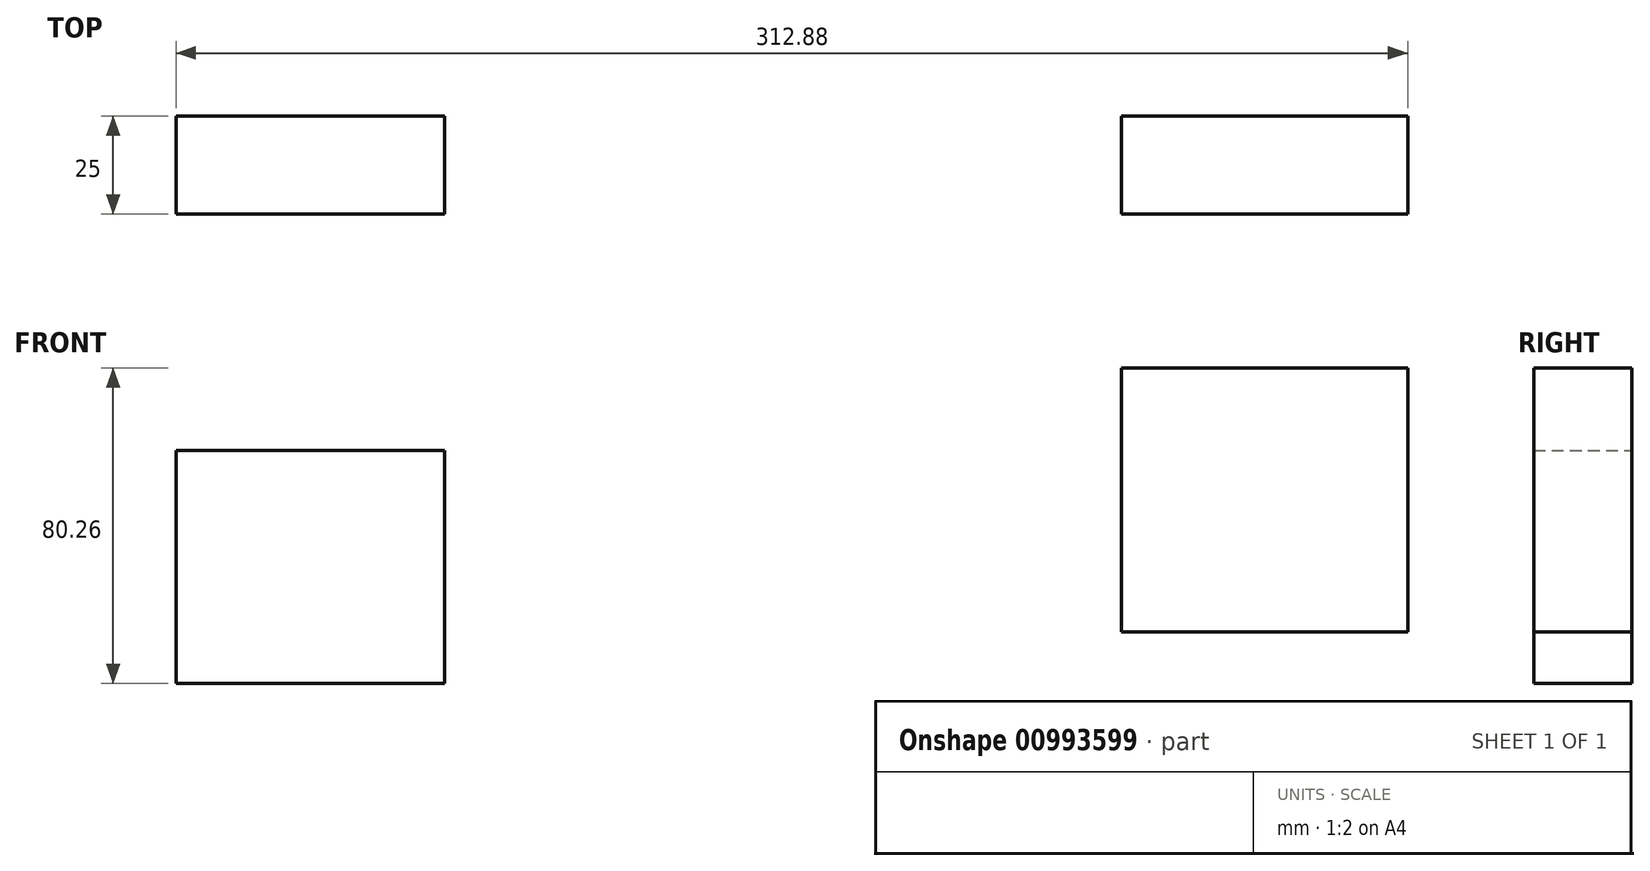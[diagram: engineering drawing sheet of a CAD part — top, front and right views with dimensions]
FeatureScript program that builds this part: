
annotation { "Feature Type Name" : "Feature", "Feature Type Description" : "" }
export const myFeature = defineFeature(function(context is Context, id is Id, definition is map)
    precondition{}
    {
        {
            var Q0;
            Q0=qCreatedBy(makeId("Front.planeOp"),FACE);
            var sketch = newSketch(context, id + "F0", { "sketchPlane" : qUnion([Q0])});
            skLineSegment(sketch, "E0.bottom", {"start": v(-157.25, 3.45) * mm, "end": v(-89.1, 3.45) * mm});
            skLineSegment(sketch, "E0.top", {"start": v(-157.25, 62.72) * mm, "end": v(-89.1, 62.72) * mm});
            skLineSegment(sketch, "E0.left", {"start": v(-157.25, 3.45) * mm, "end": v(-157.25, 62.72) * mm});
            skLineSegment(sketch, "E0.right", {"start": v(-89.1, 3.45) * mm, "end": v(-89.1, 62.72) * mm});
            skPoint(sketch, "E0.middle", {"position": v(-123.17, 33.09) * mm});
            skLineSegment(sketch, "E1.bottom", {"start": v(82.92, 16.64) * mm, "end": v(155.63, 16.64) * mm});
            skLineSegment(sketch, "E1.top", {"start": v(82.92, 83.7) * mm, "end": v(155.63, 83.7) * mm});
            skLineSegment(sketch, "E1.left", {"start": v(82.92, 16.64) * mm, "end": v(82.92, 83.7) * mm});
            skLineSegment(sketch, "E1.right", {"start": v(155.63, 16.64) * mm, "end": v(155.63, 83.7) * mm});
            skPoint(sketch, "E1.middle", {"position": v(119.28, 50.17) * mm});
            skSolve(sketch);
        }
        {
            var Q0;
            Q0=makeQuery(id+"F0.imprint","IMPRINT",FACE,{"disambiguationData":[TD([[makeQuery(id+"F0.imprint","IMPRINT",EDGE,{"derivedFrom":sQuery(id+"F0.wireOp",EDGE,"E0.bottom")}),1.0]])]});
            var Q1;
            Q1=makeQuery(id+"F0.imprint","IMPRINT",FACE,{"disambiguationData":[TD([[makeQuery(id+"F0.imprint","IMPRINT",EDGE,{"derivedFrom":sQuery(id+"F0.wireOp",EDGE,"E1.bottom")}),1.0]])]});
            extrude(context, id + "F1", {"entities" : qUnion([Q0, Q1]), "depth" : 25 * mm, "offsetDistance" : 25 * mm});
        }
    });
